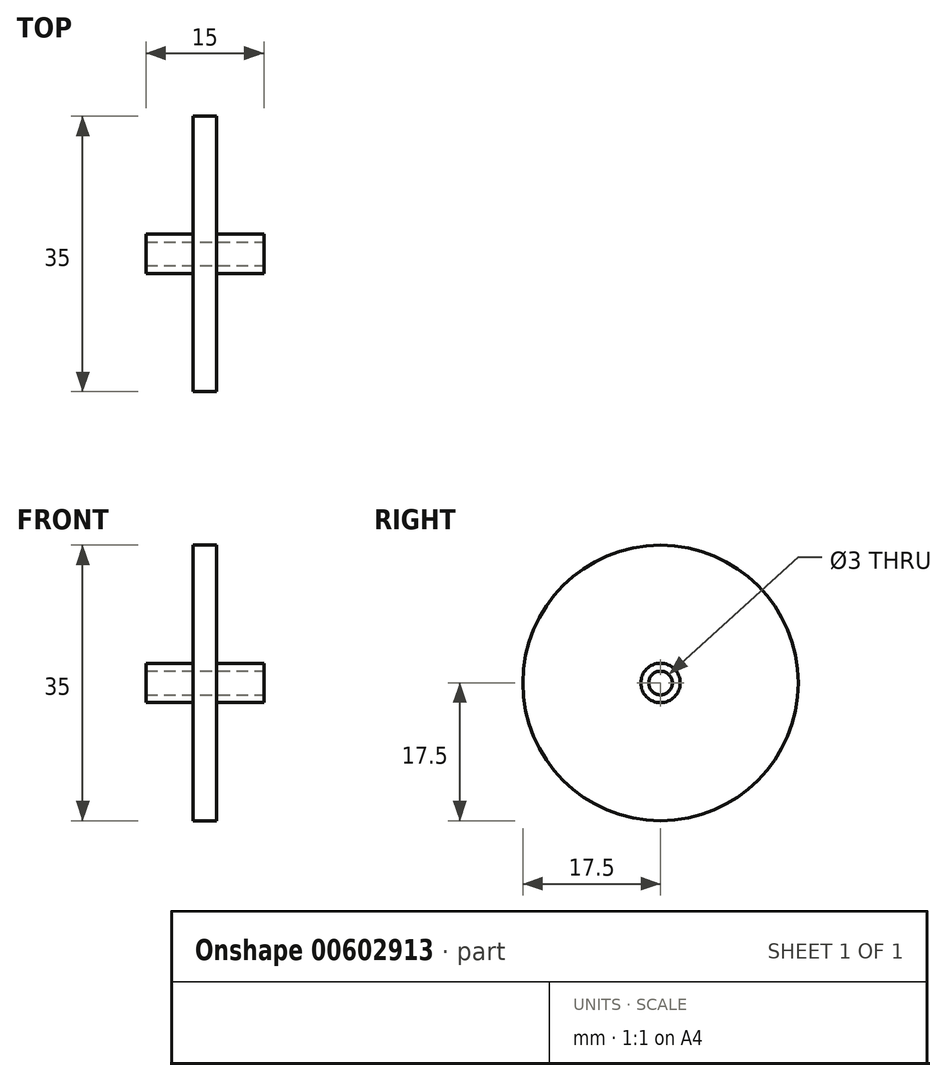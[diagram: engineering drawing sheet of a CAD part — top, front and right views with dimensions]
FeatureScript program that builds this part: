
annotation { "Feature Type Name" : "Feature", "Feature Type Description" : "" }
export const myFeature = defineFeature(function(context is Context, id is Id, definition is map)
    precondition{}
    {
        {
            var Q0;
            Q0=qCreatedBy(makeId("Right.planeOp"),FACE);
            var sketch = newSketch(context, id + "F0", { "sketchPlane" : qUnion([Q0])});
            skCircle(sketch, "E0", {"center": v(0, 0) * mm, "radius": 20 * mm});
            skSolve(sketch);
        }
        {
            var Q0;
            Q0=makeQuery(id+"F0.imprint","IMPRINT",FACE,{"disambiguationData":[TD([[makeQuery(id+"F0.imprint","IMPRINT",EDGE,{"derivedFrom":sQuery(id+"F0.wireOp",EDGE,"E0")}),1.0]])]});
            extrude(context, id + "F1", {"entities" : qUnion([Q0]), "depth" : 15 * mm, "offsetDistance" : 25 * mm});
        }
        {
            var Q0;
            Q0=makeQuery(id+"F1.opExtrude","CAP_FACE",FACE,{"disambiguationData":[OSD([sQuery(id+"F0.wireOp",EDGE,"E0")])],"isStart":false});
            var sketch = newSketch(context, id + "F2", { "sketchPlane" : qUnion([Q0])});
            skCircle(sketch, "E1", {"center": v(0, 0) * mm, "radius": 17.5 * mm});
            skCircle(sketch, "E2", {"center": v(0, 0) * mm, "radius": 2.5 * mm});
            skCircle(sketch, "E3", {"center": v(0, 0) * mm, "radius": 1.5 * mm});
            skSolve(sketch);
        }
        {
            var Q0;
            Q0=makeQuery(id+"F2.imprint","IMPRINT",FACE,{"disambiguationData":[TD([[makeQuery(id+"F2.imprint","IMPRINT",EDGE,{"derivedFrom":sQuery(id+"F2.wireOp",EDGE,"E1")}),1.0]])]});
            extrude(context, id + "F3", {"entities" : qUnion([Q0]), "operationType" : NewBodyOperationType.REMOVE, "oppositeDirection" : true, "depth" : 6 * mm, "offsetDistance" : 25 * mm});
        }
        {
            var Q0;
            Q0=makeQuery(id+"F3.boolean.opBoolean","SPLIT",FACE,{"disambiguationData":[TD([makeQuery(id+"F3.opExtrude","SWEPT_FACE",FACE,{"disambiguationData":[OSD([sQuery(id+"F2.wireOp",EDGE,"E2")])]})])],"derivedFrom":makeQuery(id+"F1.opExtrude","CAP_FACE",FACE,{"disambiguationData":[OSD([sQuery(id+"F0.wireOp",EDGE,"E0")])],"isStart":false})});
            var sketch = newSketch(context, id + "F4", { "sketchPlane" : qUnion([Q0])});
            skCircle(sketch, "E4", {"center": v(0, 0) * mm, "radius": 1.5 * mm});
            skSolve(sketch);
        }
        {
            var Q0;
            Q0=makeQuery(id+"F4.imprint","IMPRINT",FACE,{"disambiguationData":[TD([[makeQuery(id+"F4.imprint","IMPRINT",EDGE,{"derivedFrom":sQuery(id+"F4.wireOp",EDGE,"E4")}),1.0]])]});
            extrude(context, id + "F5", {"entities" : qUnion([Q0]), "operationType" : NewBodyOperationType.REMOVE, "oppositeDirection" : true, "depth" : 25 * mm, "offsetDistance" : 25 * mm});
        }
        {
            var Q0;
            Q0=makeQuery(id+"F1.opExtrude","CAP_FACE",FACE,{"disambiguationData":[OSD([sQuery(id+"F0.wireOp",EDGE,"E0")])],"isStart":true});
            var sketch = newSketch(context, id + "F6", { "sketchPlane" : qUnion([Q0])});
            skCircle(sketch, "E5", {"center": v(0, 0) * mm, "radius": 2.5 * mm});
            skCircle(sketch, "E6", {"center": v(0, 0) * mm, "radius": 17.5 * mm});
            skSolve(sketch);
        }
        {
            var Q0;
            Q0=makeQuery(id+"F6.imprint","IMPRINT",FACE,{"disambiguationData":[TD([[makeQuery(id+"F6.imprint","IMPRINT",EDGE,{"derivedFrom":sQuery(id+"F6.wireOp",EDGE,"E5")}),-1.0]])]});
            extrude(context, id + "F7", {"entities" : qUnion([Q0]), "operationType" : NewBodyOperationType.REMOVE, "oppositeDirection" : true, "depth" : 6 * mm, "offsetDistance" : 25 * mm});
        }
        {
            var Q0;
            {var subQ0=sQuery(id+"F0.wireOp",EDGE,"E0");Q0=makeQuery(id+"F3.boolean.opBoolean","SPLIT",FACE,{"disambiguationData":[TD([makeQuery(id+"F1.opExtrude","SWEPT_FACE",FACE,{"disambiguationData":[OSD([subQ0])]})])],"derivedFrom":makeQuery(id+"F1.opExtrude","CAP_FACE",FACE,{"disambiguationData":[OSD([subQ0])],"isStart":false})});}
            extrude(context, id + "F8", {"entities" : qUnion([Q0]), "operationType" : NewBodyOperationType.REMOVE, "oppositeDirection" : true, "depth" : 25 * mm, "offsetDistance" : 25 * mm});
        }
    });
